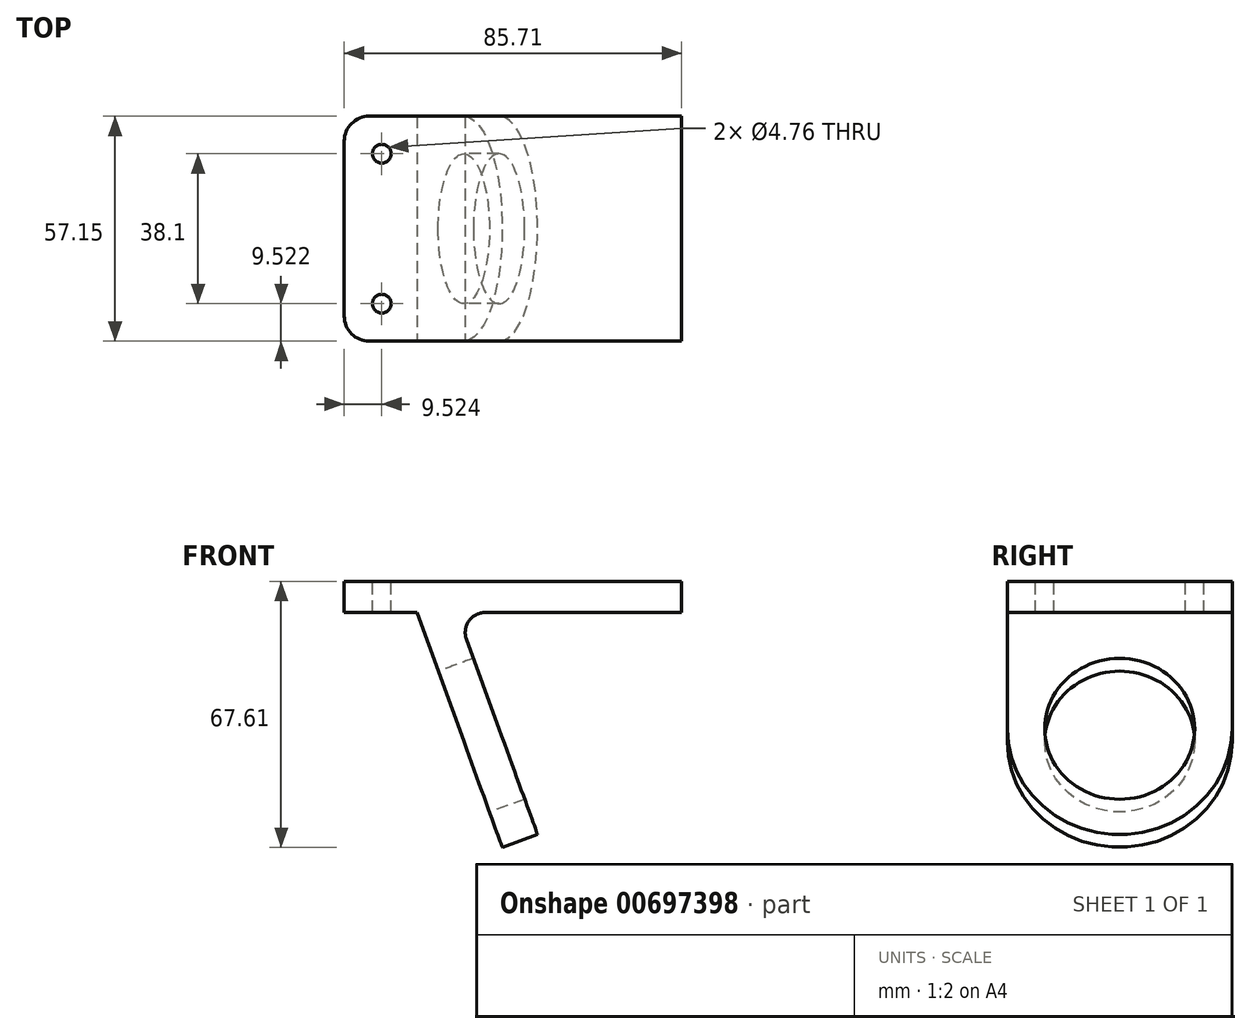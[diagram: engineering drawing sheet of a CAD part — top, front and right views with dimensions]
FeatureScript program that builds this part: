
annotation { "Feature Type Name" : "Feature", "Feature Type Description" : "" }
export const myFeature = defineFeature(function(context is Context, id is Id, definition is map)
    precondition{}
    {
        {
            var Q0;
            Q0=qCreatedBy(makeId("Top.planeOp"),FACE);
            var sketch = newSketch(context, id + "F0", { "sketchPlane" : qUnion([Q0])});
            skCircle(sketch, "E0", {"center": v(-14.9, 23.92) * mm, "radius": 2.38 * mm});
            skLineSegment(sketch, "E1", {"start": v(-24.42, 27.1) * mm, "end": v(-24.42, -17.35) * mm});
            skLineSegment(sketch, "E2", {"start": v(-18.07, -23.7) * mm, "end": v(61.3, -23.7) * mm});
            skLineSegment(sketch, "E3", {"start": v(61.3, -23.7) * mm, "end": v(61.3, 33.45) * mm});
            skLineSegment(sketch, "E4", {"start": v(61.3, 33.45) * mm, "end": v(-18.07, 33.45) * mm});
            skLineSegment(sketch, "E5", {"start": v(-24.42, 4.87) * mm, "end": v(61.3, 4.87) * mm, "construction": true});
            skCircle(sketch, "E6.MirrorC", {"center": v(-14.9, -14.18) * mm, "radius": 2.38 * mm});
            skPoint(sketch, "E7.visualSharp", {"position": v(-24.42, 33.45) * mm});
            skArc(sketch, "E7.filletArc", {"start": v(-18.07, 33.45) * mm, "mid": v(-22.56, 31.59) * mm, "end": v(-24.42, 27.1) * mm});
            skPoint(sketch, "E8.visualSharp", {"position": v(-24.42, -23.7) * mm});
            skArc(sketch, "E8.filletArc", {"start": v(-24.42, -17.35) * mm, "mid": v(-22.56, -21.84) * mm, "end": v(-18.07, -23.7) * mm});
            skSolve(sketch);
        }
        {
            var Q0;
            Q0=makeQuery(id+"F0.imprint","IMPRINT",FACE,{"disambiguationData":[TD([[makeQuery(id+"F0.imprint","IMPRINT",EDGE,{"derivedFrom":sQuery(id+"F0.wireOp",EDGE,"E0")}),-1.0]])]});
            extrude(context, id + "F1", {"entities" : qUnion([Q0]), "oppositeDirection" : true, "depth" : 7.94 * mm, "offsetDistance" : 25.4 * mm});
        }
        {
            var Q0;
            Q0=makeQuery(id+"F1.opExtrude","SWEPT_FACE",FACE,{"disambiguationData":[OSD([sQuery(id+"F0.wireOp",EDGE,"E2")])]});
            var sketch = newSketch(context, id + "F2", { "sketchPlane" : qUnion([Q0])});
            skLineSegment(sketch, "E9", {"start": v(-6, -7.94) * mm, "end": v(15.72, -67.6) * mm});
            skLineSegment(sketch, "E10", {"start": v(15.72, -67.6) * mm, "end": v(24.67, -64.35) * mm});
            skLineSegment(sketch, "E11", {"start": v(24.67, -64.35) * mm, "end": v(4.14, -7.94) * mm});
            skSolve(sketch);
        }
        {
            var Q0;
            {var subQ0=sQuery(id+"F2.wireOp",EDGE,"E9");Q0=makeQuery(id+"F2.imprint","IMPRINT",FACE,{"disambiguationData":[TD([[makeQuery(id+"F2.imprint","IMPRINT",EDGE,{"derivedFrom":subQ0}),1.0]])]});}
            extrude(context, id + "F3", {"entities" : qUnion([Q0]), "operationType" : NewBodyOperationType.ADD, "oppositeDirection" : true, "depth" : 57.15 * mm, "offsetDistance" : 25.4 * mm});
        }
        {
            var Q0;
            Q0=makeQuery(id+"F3.opExtrude","SWEPT_FACE",FACE,{"disambiguationData":[OSD([sQuery(id+"F2.wireOp",EDGE,"E9")])]});
            var sketch = newSketch(context, id + "F4", { "sketchPlane" : qUnion([Q0])});
            skLineSegment(sketch, "E12", {"start": v(-4.87, -68.9) * mm, "end": v(-4.87, -5.4) * mm, "construction": true});
            skCircle(sketch, "E13", {"center": v(-4.87, -40.33) * mm, "radius": 19.05 * mm});
            skArc(sketch, "E14", {"start": v(-33.45, -40.33) * mm, "mid": v(-4.87, -68.9) * mm, "end": v(23.7, -40.33) * mm});
            skLineSegment(sketch, "E15", {"start": v(-33.45, -40.33) * mm, "end": v(23.7, -40.33) * mm, "construction": true});
            skSolve(sketch);
        }
        {
            var Q0;
            Q0=makeQuery(id+"F4.imprint","IMPRINT",FACE,{"disambiguationData":[TD([[makeQuery(id+"F4.imprint","IMPRINT",EDGE,{"derivedFrom":sQuery(id+"F4.wireOp",EDGE,"E13")}),1.0]])]});
            var Q1;
            {var subQ0=sQuery(id+"F4.wireOp",EDGE,"E14");var subQ1=sQuery(id+"F2.wireOp",EDGE,"E9");var subQ2=makeQuery(id+"F3.opExtrude","CAP_EDGE",EDGE,{"disambiguationData":[OSD([subQ1])],"isStart":false});var subQ3=makeQuery(id+"F4.imprint","INTERSECT",VERTEX,{"derivedFrom":[subQ2,subQ0]});Q1=makeQuery(id+"F4.imprint","IMPRINT",FACE,{"disambiguationData":[TD([[makeQuery(id+"F4.imprint","IMPRINT",EDGE,{"disambiguationData":[TD([[subQ3,-1.0]])],"derivedFrom":subQ0}),-1.0]])]});}
            var Q2;
            {var subQ0=sQuery(id+"F4.wireOp",EDGE,"E14");var subQ1=sQuery(id+"F2.wireOp",EDGE,"E9");var subQ2=makeQuery(id+"F3.opExtrude","CAP_EDGE",EDGE,{"disambiguationData":[OSD([subQ1])],"isStart":true});var subQ3=makeQuery(id+"F4.imprint","INTERSECT",VERTEX,{"derivedFrom":[subQ2,subQ0]});Q2=makeQuery(id+"F4.imprint","IMPRINT",FACE,{"disambiguationData":[TD([[makeQuery(id+"F4.imprint","IMPRINT",EDGE,{"disambiguationData":[TD([[subQ3,1.0]])],"derivedFrom":subQ0}),-1.0]])]});}
            extrude(context, id + "F5", {"entities" : qUnion([Q0, Q1, Q2]), "operationType" : NewBodyOperationType.REMOVE, "endBound" : BoundingType.UP_TO_NEXT, "oppositeDirection" : true, "depth" : 25.4 * mm, "offsetDistance" : 25.4 * mm});
        }
        {
            var Q0;
            Q0=makeQuery(id+"F3.opExtrude","SWEPT_EDGE",EDGE,{"disambiguationData":[OSD([sQuery(id+"F0.wireOp",EDGE,"E2"),sQuery(id+"F2.wireOp",EDGE,"E9")])]});
            var Q1;
            Q1=makeQuery(id+"F3.opExtrude","SWEPT_EDGE",EDGE,{"disambiguationData":[OSD([sQuery(id+"F0.wireOp",EDGE,"E2"),sQuery(id+"F2.wireOp",EDGE,"E11")])]});
            fillet(context, id + "F6", {"entities" : qUnion([Q0, Q1]), "radius" : 5.08 * mm, "tangentPropagation" : true, "allowEdgeOverflow" : false});
        }
    });
